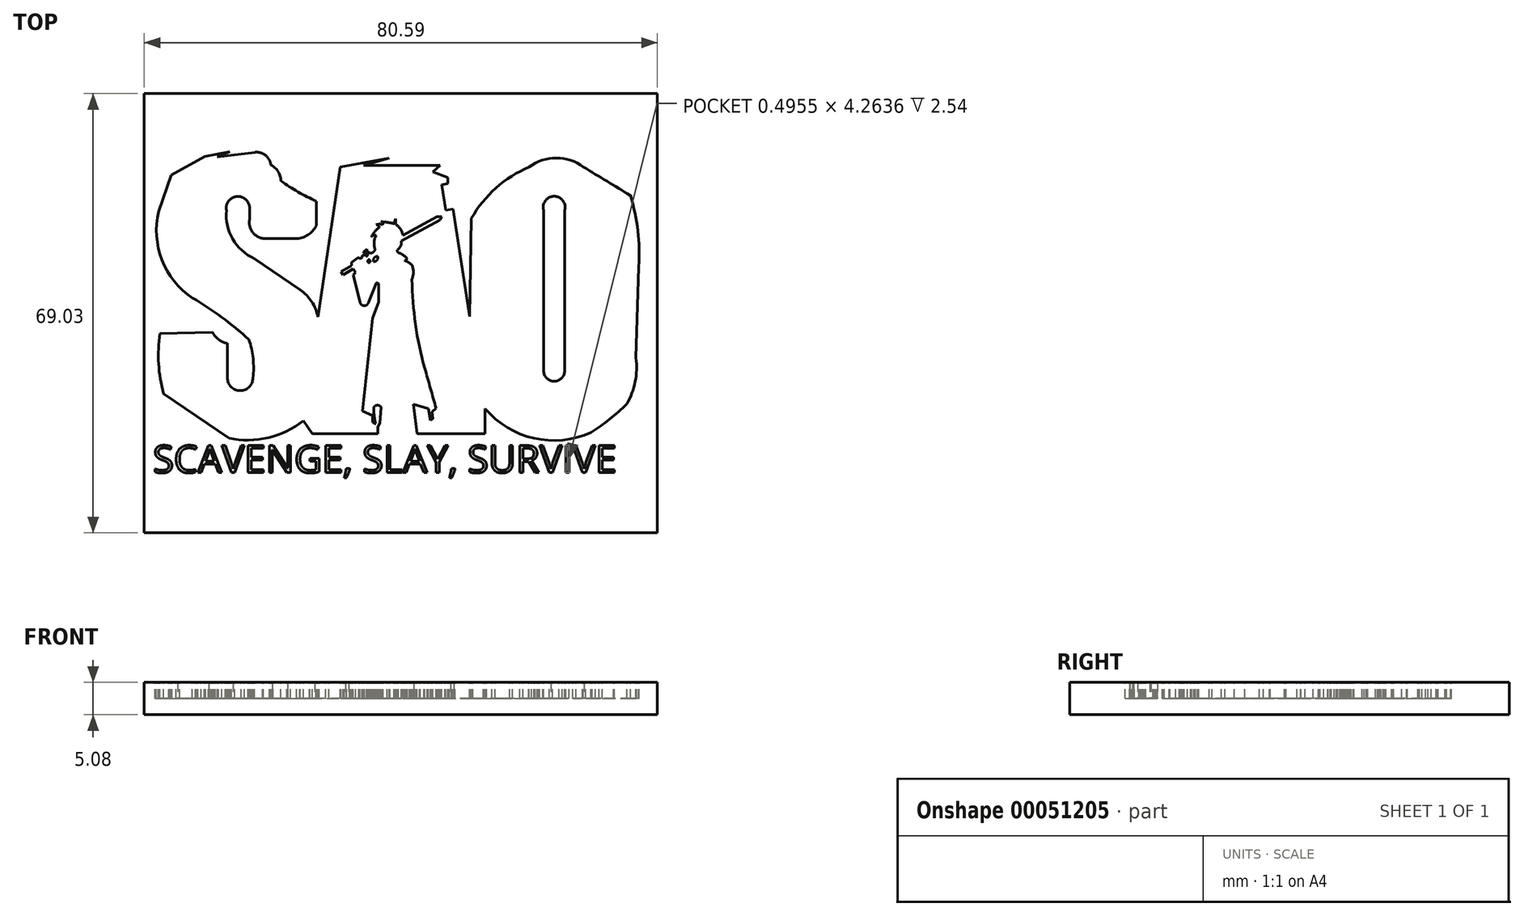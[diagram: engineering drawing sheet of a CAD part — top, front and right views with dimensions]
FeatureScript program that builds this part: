
annotation { "Feature Type Name" : "Feature", "Feature Type Description" : "" }
export const myFeature = defineFeature(function(context is Context, id is Id, definition is map)
    precondition{}
    {
        {
            var Q0;
            Q0=qCreatedBy(makeId("Top.planeOp"),FACE);
            var sketch = newSketch(context, id + "F0", { "sketchPlane" : qUnion([Q0])});
            skLineSegment(sketch, "E0.bottom", {"start": v(0, 0) * mm, "end": v(80.6, 0) * mm});
            skLineSegment(sketch, "E0.top", {"start": v(0, 69.03) * mm, "end": v(80.6, 69.03) * mm});
            skLineSegment(sketch, "E0.left", {"start": v(0, 0) * mm, "end": v(0, 69.03) * mm});
            skPoint(sketch, "E1", {"position": v(80.6, 69.03) * mm});
            skLineSegment(sketch, "E2", {"start": v(80.6, 69.03) * mm, "end": v(80.6, 0) * mm});
            skPoint(sketch, "E0.right.end.orphan", {"position": v(161.18, 69.03) * mm});
            skPoint(sketch, "E3.orphan", {"position": v(161.18, 0) * mm});
            skSolve(sketch);
        }
        {
            var Q0;
            Q0 = qSketchRegion(id + "F0", true);
            extrude(context, id + "F1", {"entities" : qUnion([Q0]), "depth" : 5.08 * mm});
        }
        {
            var Q0;
            Q0=makeQuery(id+"F1.opExtrude","CAP_FACE",FACE,{"disambiguationData":[OSD([sQuery(id+"F0.wireOp",EDGE,"E0.bottom"),sQuery(id+"F0.wireOp",EDGE,"E0.top"),sQuery(id+"F0.wireOp",EDGE,"E0.left"),sQuery(id+"F0.wireOp",EDGE,"E2")])],"isStart":false});
            var sketch = newSketch(context, id + "F2", { "sketchPlane" : qUnion([Q0])});
            skText(sketch, "E4", { "text": "SCAVENGE, SLAY, SURVIVE", "fontName": "OpenSans-Regular.ttf"});
            skLineSegment(sketch, "E5", {"start": v(3.04, 21.87) * mm, "end": v(13.3, 14.87) * mm});
            skArc(sketch, "E6", {"start": v(2.48, 31.33) * mm, "mid": v(2.27, 26.57) * mm, "end": v(3.04, 21.87) * mm});
            skArc(sketch, "E7", {"start": v(10.75, 31.5) * mm, "mid": v(11.71, 30.38) * mm, "end": v(13.07, 29.8) * mm});
            skLineSegment(sketch, "E8", {"start": v(2.48, 31.33) * mm, "end": v(10.75, 31.5) * mm});
            skArc(sketch, "E9", {"start": v(13.3, 14.87) * mm, "mid": v(19.45, 14.95) * mm, "end": v(25, 17.63) * mm});
            skLineSegment(sketch, "E10", {"start": v(13.07, 29.8) * mm, "end": v(13.07, 24.36) * mm});
            skArc(sketch, "E11", {"start": v(13.07, 24.36) * mm, "mid": v(15.07, 22.35) * mm, "end": v(17.08, 24.36) * mm});
            skArc(sketch, "E12", {"start": v(17.08, 24.36) * mm, "mid": v(17.1, 27.4) * mm, "end": v(16.43, 30.38) * mm});
            skArc(sketch, "E13", {"start": v(16.43, 30.38) * mm, "mid": v(12.17, 33.88) * mm, "end": v(7.57, 36.93) * mm});
            skArc(sketch, "E14", {"start": v(2.27, 50.5) * mm, "mid": v(2.8, 42.89) * mm, "end": v(7.57, 36.93) * mm});
            skLineSegment(sketch, "E15", {"start": v(2.27, 50.5) * mm, "end": v(4.27, 56.25) * mm});
            skLineSegment(sketch, "E16", {"start": v(4.27, 56.25) * mm, "end": v(9.5, 59.14) * mm});
            skLineSegment(sketch, "E17", {"start": v(9.5, 59.14) * mm, "end": v(13.48, 59.92) * mm});
            skLineSegment(sketch, "E18", {"start": v(13.48, 59.92) * mm, "end": v(11.5, 59.08) * mm});
            skPoint(sketch, "E18.endSnap0", {"position": v(11.5, 59.53) * mm});
            skLineSegment(sketch, "E19", {"start": v(11.5, 59.08) * mm, "end": v(17.4, 59.8) * mm});
            skArc(sketch, "E20", {"start": v(19.88, 57.81) * mm, "mid": v(19.05, 59.33) * mm, "end": v(17.4, 59.8) * mm});
            skArc(sketch, "E21", {"start": v(21.47, 55.3) * mm, "mid": v(21.02, 56.78) * mm, "end": v(19.88, 57.81) * mm});
            skArc(sketch, "E22", {"start": v(21.47, 55.3) * mm, "mid": v(24.17, 53.58) * mm, "end": v(27.03, 52.12) * mm});
            skLineSegment(sketch, "E23", {"start": v(27.03, 52.12) * mm, "end": v(27.03, 48.32) * mm});
            skLineSegment(sketch, "E24", {"start": v(19.05, 46.24) * mm, "end": v(23.72, 46.24) * mm});
            skArc(sketch, "E25", {"start": v(23.72, 46.24) * mm, "mid": v(25.68, 46.8) * mm, "end": v(27.03, 48.32) * mm});
            skArc(sketch, "E26", {"start": v(16.54, 49.17) * mm, "mid": v(17.12, 47.13) * mm, "end": v(19.05, 46.24) * mm});
            skArc(sketch, "E27", {"start": v(16.54, 50.75) * mm, "mid": v(14.68, 52.86) * mm, "end": v(12.9, 50.68) * mm});
            skLineSegment(sketch, "E28", {"start": v(16.54, 50.75) * mm, "end": v(16.54, 49.17) * mm});
            skArc(sketch, "E29", {"start": v(12.9, 50.68) * mm, "mid": v(13.88, 46.18) * mm, "end": v(17.31, 43.1) * mm});
            skArc(sketch, "E30", {"start": v(27.28, 33.93) * mm, "mid": v(26.3, 36.34) * mm, "end": v(24.5, 38.2) * mm});
            skLineSegment(sketch, "E31", {"start": v(17.31, 43.1) * mm, "end": v(24.5, 38.2) * mm});
            skLineSegment(sketch, "E32", {"start": v(25, 17.63) * mm, "end": v(26.4, 15.6) * mm});
            skLineSegment(sketch, "E33", {"start": v(26.4, 15.6) * mm, "end": v(36.71, 15.6) * mm});
            skLineSegment(sketch, "E34", {"start": v(36.71, 15.6) * mm, "end": v(36.71, 16.64) * mm});
            skLineSegment(sketch, "E35", {"start": v(36.71, 16.64) * mm, "end": v(37, 17.23) * mm});
            skLineSegment(sketch, "E36", {"start": v(37, 17.23) * mm, "end": v(37.2, 19.73) * mm});
            skArc(sketch, "E37", {"start": v(37.2, 19.73) * mm, "mid": v(36.62, 20.07) * mm, "end": v(36.05, 19.73) * mm});
            skArc(sketch, "E38", {"start": v(36.05, 19.73) * mm, "mid": v(36.11, 18.44) * mm, "end": v(36.34, 17.17) * mm});
            skArc(sketch, "E39", {"start": v(35.89, 17.38) * mm, "mid": v(36.1, 17.23) * mm, "end": v(36.34, 17.17) * mm});
            skLineSegment(sketch, "E40", {"start": v(35.89, 17.38) * mm, "end": v(35.89, 18.46) * mm});
            skLineSegment(sketch, "E41", {"start": v(35.89, 18.46) * mm, "end": v(34.25, 19.14) * mm});
            skLineSegment(sketch, "E42", {"start": v(34.25, 19.14) * mm, "end": v(35.88, 33.72) * mm});
            skLineSegment(sketch, "E43", {"start": v(35.88, 33.72) * mm, "end": v(36.82, 36.31) * mm});
            skLineSegment(sketch, "E44", {"start": v(36.82, 36.31) * mm, "end": v(36.82, 39.05) * mm});
            skArc(sketch, "E45", {"start": v(36.82, 39.05) * mm, "mid": v(36.58, 39.29) * mm, "end": v(36.34, 39.05) * mm});
            skArc(sketch, "E46", {"start": v(33.88, 36.28) * mm, "mid": v(34.53, 35.7) * mm, "end": v(35.23, 36.22) * mm});
            skLineSegment(sketch, "E47", {"start": v(36.34, 39.05) * mm, "end": v(35.23, 36.22) * mm});
            skLineSegment(sketch, "E48", {"start": v(33.88, 36.28) * mm, "end": v(32.83, 40.52) * mm});
            skLineSegment(sketch, "E49", {"start": v(32.83, 40.52) * mm, "end": v(33.2, 40.9) * mm});
            skLineSegment(sketch, "E50", {"start": v(33.2, 40.9) * mm, "end": v(32.84, 41.5) * mm});
            skLineSegment(sketch, "E51", {"start": v(32.84, 41.5) * mm, "end": v(31.21, 40.56) * mm});
            skLineSegment(sketch, "E52", {"start": v(31.21, 40.56) * mm, "end": v(30.91, 41.07) * mm});
            skLineSegment(sketch, "E53", {"start": v(30.91, 41.07) * mm, "end": v(32.55, 42.01) * mm});
            skLineSegment(sketch, "E54", {"start": v(32.55, 42.01) * mm, "end": v(32.55, 42.51) * mm});
            skLineSegment(sketch, "E55", {"start": v(32.55, 42.51) * mm, "end": v(33.7, 43.32) * mm});
            skArc(sketch, "E56", {"start": v(33.7, 43.32) * mm, "mid": v(34.02, 43.12) * mm, "end": v(34.21, 43.46) * mm});
            skArc(sketch, "E57", {"start": v(34.92, 43.46) * mm, "mid": v(34.57, 43.68) * mm, "end": v(34.21, 43.46) * mm});
            skArc(sketch, "E58", {"start": v(34.92, 43.46) * mm, "mid": v(35.08, 43.7) * mm, "end": v(34.92, 43.96) * mm});
            skLineSegment(sketch, "E59", {"start": v(34.92, 43.96) * mm, "end": v(34.44, 43.96) * mm});
            skLineSegment(sketch, "E60", {"start": v(34.44, 43.96) * mm, "end": v(34.44, 44.17) * mm});
            skLineSegment(sketch, "E61", {"start": v(34.44, 44.17) * mm, "end": v(34.95, 44.62) * mm});
            skArc(sketch, "E62", {"start": v(34.95, 44.62) * mm, "mid": v(35.59, 43.98) * mm, "end": v(36.23, 44.62) * mm});
            skArc(sketch, "E63", {"start": v(36.42, 46.74) * mm, "mid": v(36.11, 45.7) * mm, "end": v(36.23, 44.62) * mm});
            skArc(sketch, "E64", {"start": v(36.42, 46.74) * mm, "mid": v(36.02, 46.76) * mm, "end": v(35.7, 46.51) * mm});
            skArc(sketch, "E65", {"start": v(36.93, 48.02) * mm, "mid": v(36.22, 47.34) * mm, "end": v(35.7, 46.51) * mm});
            skArc(sketch, "E66", {"start": v(36.93, 48.02) * mm, "mid": v(36.74, 48.31) * mm, "end": v(36.42, 48.44) * mm});
            skArc(sketch, "E67", {"start": v(37.46, 48.44) * mm, "mid": v(36.94, 48.51) * mm, "end": v(36.42, 48.44) * mm});
            skArc(sketch, "E68", {"start": v(37.46, 48.44) * mm, "mid": v(37.42, 48.78) * mm, "end": v(37.1, 48.9) * mm});
            skArc(sketch, "E69", {"start": v(39.25, 48.6) * mm, "mid": v(38.19, 48.8) * mm, "end": v(37.1, 48.9) * mm});
            skLineSegment(sketch, "E70", {"start": v(39.25, 48.6) * mm, "end": v(39.46, 49.34) * mm});
            skLineSegment(sketch, "E71", {"start": v(39.46, 49.34) * mm, "end": v(39.46, 48.52) * mm});
            skArc(sketch, "E72", {"start": v(40.63, 46.78) * mm, "mid": v(40.22, 47.77) * mm, "end": v(39.46, 48.52) * mm});
            skLineSegment(sketch, "E73", {"start": v(40.63, 46.78) * mm, "end": v(45.94, 49.67) * mm});
            skLineSegment(sketch, "E74", {"start": v(45.94, 49.67) * mm, "end": v(46.72, 49.67) * mm});
            skLineSegment(sketch, "E75", {"start": v(46.72, 49.67) * mm, "end": v(46.45, 49.19) * mm});
            skLineSegment(sketch, "E76", {"start": v(46.45, 49.19) * mm, "end": v(40.38, 45.87) * mm});
            skArc(sketch, "E77", {"start": v(39.77, 44.5) * mm, "mid": v(40.28, 45.1) * mm, "end": v(40.38, 45.87) * mm});
            skArc(sketch, "E78", {"start": v(39.77, 44.5) * mm, "mid": v(39.77, 44.23) * mm, "end": v(39.94, 44) * mm});
            skArc(sketch, "E79", {"start": v(41.3, 43.14) * mm, "mid": v(40.67, 43.66) * mm, "end": v(39.94, 44) * mm});
            skArc(sketch, "E80", {"start": v(36.67, 43.44) * mm, "mid": v(36.11, 43.22) * mm, "end": v(36.03, 42.62) * mm});
            skArc(sketch, "E81", {"start": v(36.03, 42.62) * mm, "mid": v(36.56, 42.86) * mm, "end": v(36.67, 43.44) * mm});
            skArc(sketch, "E82", {"start": v(35.32, 42.42) * mm, "mid": v(35.47, 42.69) * mm, "end": v(35.3, 42.95) * mm});
            skArc(sketch, "E83", {"start": v(35.3, 42.95) * mm, "mid": v(35.1, 42.68) * mm, "end": v(35.32, 42.42) * mm});
            skArc(sketch, "E84", {"start": v(40.87, 42.81) * mm, "mid": v(41.15, 42.89) * mm, "end": v(41.3, 43.14) * mm});
            skArc(sketch, "E85", {"start": v(42.05, 42.1) * mm, "mid": v(41.49, 42.5) * mm, "end": v(40.87, 42.81) * mm});
            skArc(sketch, "E86", {"start": v(42.05, 39.84) * mm, "mid": v(42.26, 40.97) * mm, "end": v(42.05, 42.1) * mm});
            skArc(sketch, "E87", {"start": v(42.05, 39.84) * mm, "mid": v(42.6, 32.78) * mm, "end": v(44.05, 25.86) * mm});
            skArc(sketch, "E88", {"start": v(45.84, 19.55) * mm, "mid": v(44.96, 22.7) * mm, "end": v(44.05, 25.86) * mm});
            skLineSegment(sketch, "E89", {"start": v(45.84, 19.55) * mm, "end": v(45.2, 18.99) * mm});
            skLineSegment(sketch, "E90", {"start": v(45.2, 18.99) * mm, "end": v(45.33, 17.94) * mm});
            skLineSegment(sketch, "E91", {"start": v(45.33, 17.94) * mm, "end": v(44.96, 17.7) * mm});
            skLineSegment(sketch, "E92", {"start": v(44.96, 17.7) * mm, "end": v(44.64, 19.5) * mm});
            skLineSegment(sketch, "E93", {"start": v(44.64, 19.5) * mm, "end": v(42.3, 20.22) * mm});
            skLineSegment(sketch, "E94", {"start": v(42.3, 20.22) * mm, "end": v(42.82, 15.6) * mm});
            skLineSegment(sketch, "E95", {"start": v(42.82, 15.6) * mm, "end": v(53.53, 15.6) * mm});
            skLineSegment(sketch, "E96", {"start": v(53.53, 15.6) * mm, "end": v(53.53, 19.53) * mm});
            skArc(sketch, "E97", {"start": v(53.53, 19.53) * mm, "mid": v(61.22, 14.87) * mm, "end": v(70.17, 15.75) * mm});
            skArc(sketch, "E98", {"start": v(70.17, 15.75) * mm, "mid": v(73.09, 17.87) * mm, "end": v(75.8, 20.26) * mm});
            skArc(sketch, "E99", {"start": v(75.8, 20.26) * mm, "mid": v(77.1, 23.76) * mm, "end": v(77.23, 27.5) * mm});
            skArc(sketch, "E100", {"start": v(76.35, 53.02) * mm, "mid": v(72.67, 55.26) * mm, "end": v(68.97, 57.49) * mm});
            skArc(sketch, "E101", {"start": v(77.66, 41.83) * mm, "mid": v(77.53, 47.49) * mm, "end": v(76.35, 53.02) * mm});
            skLineSegment(sketch, "E102", {"start": v(77.66, 41.83) * mm, "end": v(77.23, 27.5) * mm});
            skPoint(sketch, "E103", {"position": v(62.74, 50.6) * mm});
            skPoint(sketch, "E104", {"position": v(66.01, 50.6) * mm});
            skPoint(sketch, "E105", {"position": v(66.01, 25.45) * mm});
            skPoint(sketch, "E106", {"position": v(62.74, 25.45) * mm});
            skArc(sketch, "E107", {"start": v(66.01, 50.6) * mm, "mid": v(64.38, 52.9) * mm, "end": v(62.74, 50.6) * mm});
            skLineSegment(sketch, "E108", {"start": v(62.74, 50.6) * mm, "end": v(62.74, 25.45) * mm});
            skLineSegment(sketch, "E109", {"start": v(66.01, 50.6) * mm, "end": v(66.01, 25.45) * mm});
            skArc(sketch, "E110", {"start": v(62.74, 25.45) * mm, "mid": v(64.38, 23.81) * mm, "end": v(66.01, 25.45) * mm});
            skArc(sketch, "E111", {"start": v(68.97, 57.49) * mm, "mid": v(64.7, 58.92) * mm, "end": v(60.44, 57.49) * mm});
            skArc(sketch, "E112", {"start": v(60.44, 57.49) * mm, "mid": v(55.25, 54.2) * mm, "end": v(51.4, 49.42) * mm});
            skLineSegment(sketch, "E113", {"start": v(51.1, 33.99) * mm, "end": v(51.4, 49.42) * mm});
            skLineSegment(sketch, "E114", {"start": v(51.1, 33.99) * mm, "end": v(48.51, 50.87) * mm});
            skLineSegment(sketch, "E115", {"start": v(48.51, 50.87) * mm, "end": v(47.35, 50.7) * mm});
            skLineSegment(sketch, "E116", {"start": v(47.35, 50.7) * mm, "end": v(46.74, 54.68) * mm});
            skLineSegment(sketch, "E117", {"start": v(46.74, 54.68) * mm, "end": v(47.65, 54.92) * mm});
            skLineSegment(sketch, "E118", {"start": v(47.65, 54.92) * mm, "end": v(47.65, 55.87) * mm});
            skLineSegment(sketch, "E119", {"start": v(47.65, 55.87) * mm, "end": v(45.33, 56.73) * mm});
            skLineSegment(sketch, "E120", {"start": v(45.33, 56.73) * mm, "end": v(46.45, 57.76) * mm});
            skLineSegment(sketch, "E121", {"start": v(46.45, 57.76) * mm, "end": v(34.47, 57.76) * mm});
            skLineSegment(sketch, "E122", {"start": v(34.47, 57.76) * mm, "end": v(38.44, 58.88) * mm});
            skLineSegment(sketch, "E123", {"start": v(38.44, 58.88) * mm, "end": v(30.77, 57.5) * mm});
            skLineSegment(sketch, "E124", {"start": v(30.77, 57.5) * mm, "end": v(27.28, 33.93) * mm});
            const initialGuessF2  = {"E4": [0.00137, 0.00946, 1, 0, 0.0043]};
            skSetInitialGuess(sketch, initialGuessF2);
            skSolve(sketch);
        }
        {
            var Q0;
            Q0 = qSketchRegion(id + "F2", true);
            extrude(context, id + "F3", {"entities" : qUnion([Q0]), "operationType" : NewBodyOperationType.REMOVE, "oppositeDirection" : true, "depth" : 2.54 * mm});
        }
    });
